# Revit family: Window_Curtain_Wall-Project_Out-Traco-NX_35X-Heavy_Commercial
name_source: partatom
category: Windows
revit_build: Autodesk Revit 2015 (Build: 20140905_0730(x64)
units: mm (PartAtom-declared; Revit-internal decimal feet)

## types (2) — shared parameters
Assembly Code = B2020110
CTRL Configuration Number = 5
CTRL Panel Active Frame Width = 0' - 2"
Condensation Resistance = 0.0000 ksf
Depth = 0' - 3 1/4"
Description = Heavy Commercial Historic, Project Out Window
Frame Material = Aluminum - Traco - Anodized - Bronze
Glazing Material = Glass - Traco - Clear
Glazing Thickness = 0' - 1"
Head Width = 0' - 1 1/2"
Height Maximum = 8' - 0"
Height Minimum = 4' - 6"
Jamb Width = 0' - 1 1/2"
Keynote = 08520
Manufacturer = Traco
Model = NX-3XX
Panel Configuration = Vent
Product Documentation Link = http://www.alcoa.com
Product Page URL = http://www.alcoa.com
Product data url = https://bimobject.com
Screen Material = Aluminum - Traco - Screen
Sill Width = 0' - 1 1/2"
Type Comments = Fixed/Vent with Side Lites
URL = http://www.alcoa.com
Uniform Load Deflection = 0.0000 ksf
Uniform Load Structural = 0.0000 ksf
Water Resistance = 0.0000 ksf
Width Maximum = 5' - 4"
Width Minimum = 3' - 0"

## per-type parameters (varying)
| type | CTRL Has No Vent | CTRL Has Vent |
| NX-35X - Project_Out - Fixed/Vent | No | Yes |
| NX-35X - Project_Out - Fixed | Yes | No |

## geometry (parser evidence)
native form markers: Blend x10, Sweep x13
no freeform markers — native parametric forms only
